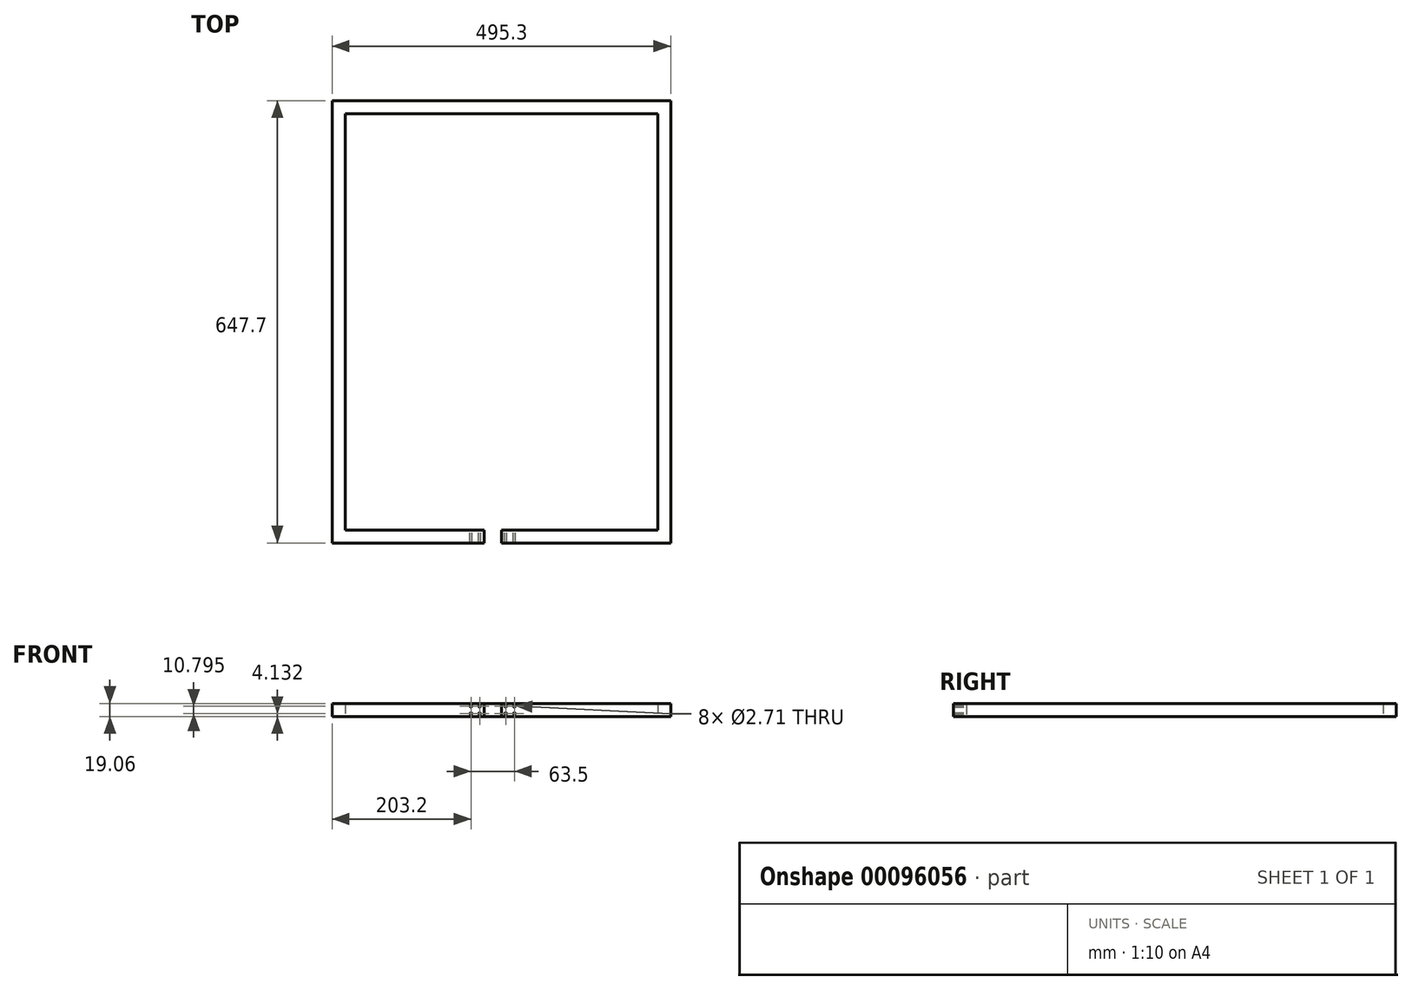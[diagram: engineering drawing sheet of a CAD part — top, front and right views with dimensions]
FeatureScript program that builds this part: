
annotation { "Feature Type Name" : "Feature", "Feature Type Description" : "" }
export const myFeature = defineFeature(function(context is Context, id is Id, definition is map)
    precondition{}
    {
        {
            var Q0;
            Q0=qCreatedBy(makeId("Top.planeOp"),FACE);
            var sketch = newSketch(context, id + "F0", { "sketchPlane" : qUnion([Q0])});
            skLineSegment(sketch, "E0", {"start": v(457.2, 0) * mm, "end": v(457.2, 609.6) * mm});
            skLineSegment(sketch, "E1", {"start": v(457.2, 609.6) * mm, "end": v(0, 609.6) * mm});
            skLineSegment(sketch, "E2", {"start": v(0, 609.6) * mm, "end": v(0, 0) * mm});
            skLineSegment(sketch, "E3.0", {"start": v(-19.05, 628.65) * mm, "end": v(-19.05, -19.05) * mm});
            skLineSegment(sketch, "E3.1", {"start": v(476.25, 628.65) * mm, "end": v(-19.05, 628.65) * mm});
            skLineSegment(sketch, "E3.2", {"start": v(476.25, -19.05) * mm, "end": v(476.25, 628.65) * mm});
            skLineSegment(sketch, "E4", {"start": v(-19.05, -19.05) * mm, "end": v(203.2, -19.05) * mm});
            skLineSegment(sketch, "E5", {"start": v(457.2, 0) * mm, "end": v(228.6, 0) * mm});
            skLineSegment(sketch, "E6", {"start": v(203.2, 0) * mm, "end": v(203.2, -19.05) * mm});
            skLineSegment(sketch, "E7", {"start": v(228.6, -19.05) * mm, "end": v(228.6, 0) * mm});
            skLineSegment(sketch, "E8.trimOffspring", {"start": v(203.2, 0) * mm, "end": v(0, 0) * mm});
            skLineSegment(sketch, "E9.trimOffspring", {"start": v(228.6, -19.05) * mm, "end": v(476.25, -19.05) * mm});
            skSolve(sketch);
        }
        {
            var Q0;
            Q0 = qSketchRegion(id + "F0", true);
            extrude(context, id + "F1", {"entities" : qUnion([Q0]), "endBound" : BoundingType.SYMMETRIC, "depth" : 19.05 * mm});
        }
        {
            var Q0;
            Q0=makeQuery(id+"F1.opExtrude","SWEPT_FACE",FACE,{"disambiguationData":[OSD([sQuery(id+"F0.wireOp",EDGE,"E5")])]});
            var sketch = newSketch(context, id + "F2", { "sketchPlane" : qUnion([Q0])});
            skCircle(sketch, "E10", {"center": v(-247.65, 5.4) * mm, "radius": 1.35 * mm});
            skLineSegment(sketch, "E11", {"start": v(-203.2, 9.53) * mm, "end": v(-228.6, 9.53) * mm, "construction": true});
            skLineSegment(sketch, "E12", {"start": v(-215.9, 9.53) * mm, "end": v(-215.9, -9.96) * mm, "construction": true});
            skCircle(sketch, "E13.0.1.0", {"center": v(-247.65, -5.4) * mm, "radius": 1.35 * mm});
            skCircle(sketch, "E13.1.0.0", {"center": v(-234.95, 5.4) * mm, "radius": 1.35 * mm});
            skCircle(sketch, "E13.1.1.0", {"center": v(-234.95, -5.4) * mm, "radius": 1.35 * mm});
            skLineSegment(sketch, "E13.direction1", {"start": v(-247.65, 5.4) * mm, "end": v(-234.95, 5.4) * mm, "construction": true});
            skLineSegment(sketch, "E13.direction2", {"start": v(-247.65, 5.4) * mm, "end": v(-247.65, -5.4) * mm, "construction": true});
            skLineSegment(sketch, "E14", {"start": v(-247.65, 0) * mm, "end": v(-228.6, 0) * mm});
            skCircle(sketch, "E15.MirrorC", {"center": v(-196.85, 5.4) * mm, "radius": 1.35 * mm});
            skCircle(sketch, "E16.MirrorC", {"center": v(-184.15, 5.4) * mm, "radius": 1.35 * mm});
            skCircle(sketch, "E17.MirrorC", {"center": v(-184.15, -5.4) * mm, "radius": 1.35 * mm});
            skCircle(sketch, "E18.MirrorC", {"center": v(-196.85, -5.4) * mm, "radius": 1.35 * mm});
            skSolve(sketch);
        }
        {
            var Q0;
            Q0 = qSketchRegion(id + "F2", true);
            extrude(context, id + "F3", {"entities" : qUnion([Q0]), "operationType" : NewBodyOperationType.REMOVE, "endBound" : BoundingType.THROUGH_ALL, "oppositeDirection" : true, "depth" : 25.4 * mm});
        }
    });
